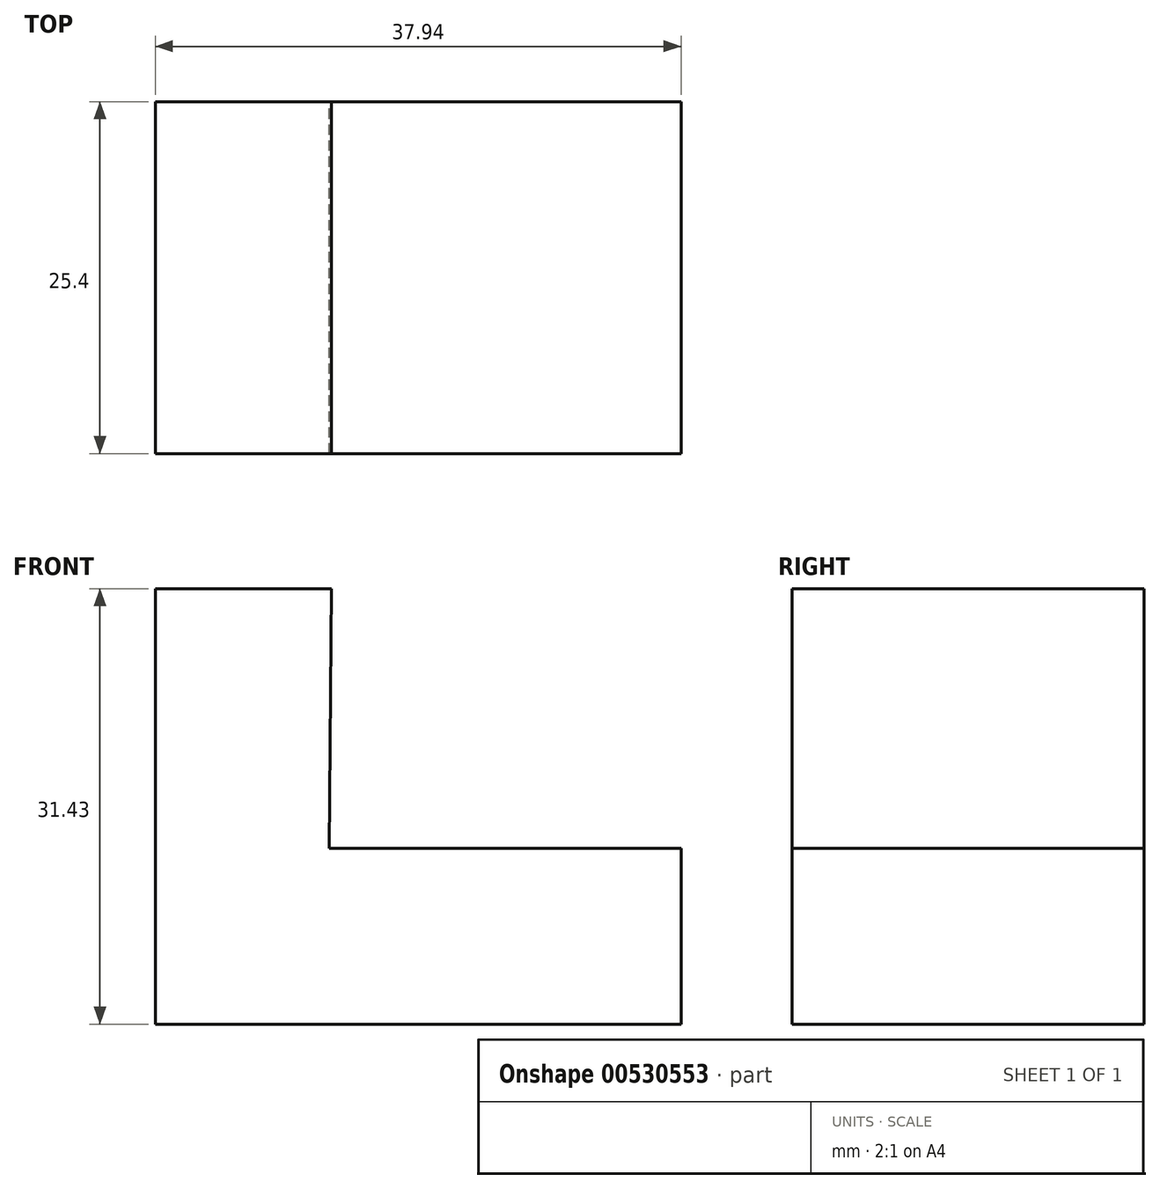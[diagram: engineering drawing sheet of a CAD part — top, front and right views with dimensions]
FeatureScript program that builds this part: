
annotation { "Feature Type Name" : "Feature", "Feature Type Description" : "" }
export const myFeature = defineFeature(function(context is Context, id is Id, definition is map)
    precondition{}
    {
        {
            var Q0;
            Q0=qCreatedBy(makeId("Front.planeOp"),FACE);
            var sketch = newSketch(context, id + "F0", { "sketchPlane" : qUnion([Q0])});
            skLineSegment(sketch, "E0", {"start": v(-49.85, 31.43) * mm, "end": v(-49.85, 0) * mm});
            skLineSegment(sketch, "E1", {"start": v(-49.85, 0) * mm, "end": v(-11.9, 0) * mm});
            skLineSegment(sketch, "E2", {"start": v(-11.9, 0) * mm, "end": v(-11.9, 12.7) * mm});
            skLineSegment(sketch, "E3", {"start": v(-11.9, 12.7) * mm, "end": v(-37.3, 12.7) * mm});
            skLineSegment(sketch, "E4", {"start": v(-49.85, 31.43) * mm, "end": v(-37.15, 31.43) * mm});
            skLineSegment(sketch, "E5", {"start": v(-37.15, 31.43) * mm, "end": v(-37.3, 12.7) * mm});
            skSolve(sketch);
        }
        {
            var Q0;
            Q0 = qSketchRegion(id + "F0", true);
            extrude(context, id + "F1", {"entities" : qUnion([Q0]), "depth" : 25.4 * mm, "offsetDistance" : 25.4 * mm});
        }
    });
